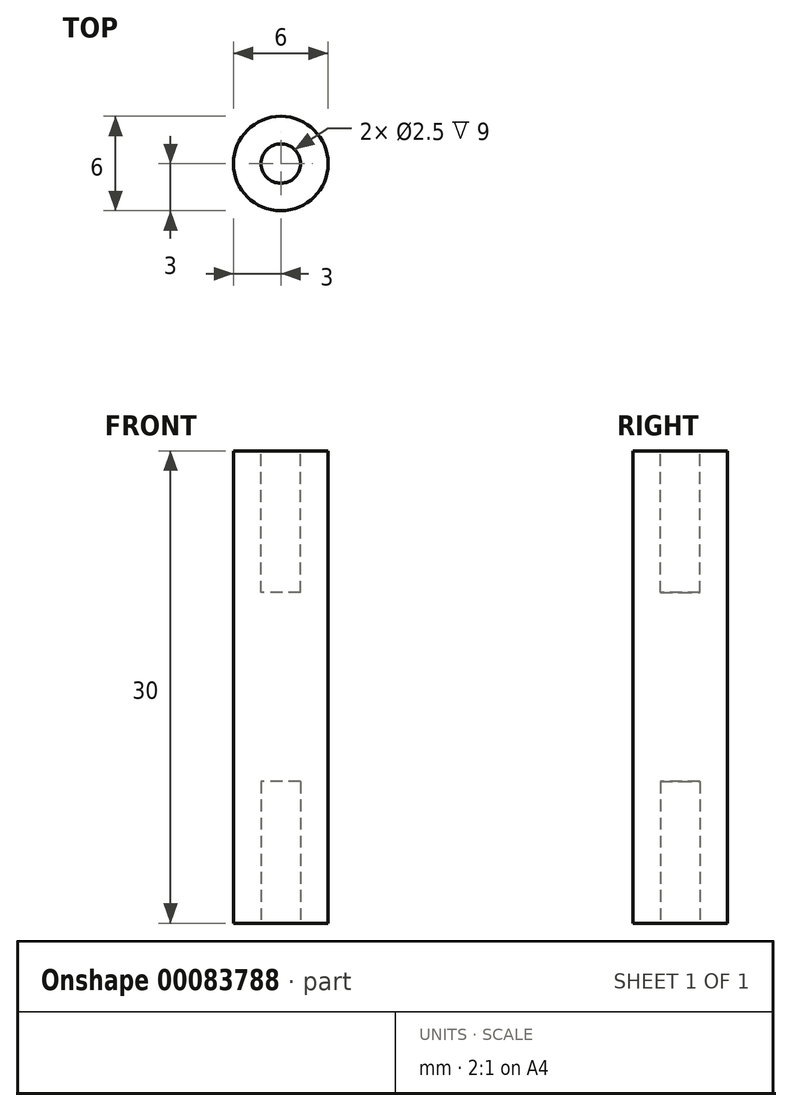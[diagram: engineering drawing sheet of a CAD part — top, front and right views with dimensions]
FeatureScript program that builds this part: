
annotation { "Feature Type Name" : "Feature", "Feature Type Description" : "" }
export const myFeature = defineFeature(function(context is Context, id is Id, definition is map)
    precondition{}
    {
        {
            var Q0;
            Q0=qCreatedBy(makeId("Top.planeOp"),FACE);
            var sketch = newSketch(context, id + "F0", { "sketchPlane" : qUnion([Q0])});
            skCircle(sketch, "E0", {"center": v(0, 0) * mm, "radius": 3 * mm});
            skCircle(sketch, "E1", {"center": v(0, 0) * mm, "radius": 1.25 * mm});
            skSolve(sketch);
        }
        {
            var Q0;
            Q0=makeQuery(id+"F0.imprint","IMPRINT",FACE,{"disambiguationData":[TD([[makeQuery(id+"F0.imprint","IMPRINT",EDGE,{"derivedFrom":sQuery(id+"F0.wireOp",EDGE,"E0")}),1.0]])]});
            var Q1;
            Q1=makeQuery(id+"F0.imprint","IMPRINT",FACE,{"disambiguationData":[TD([[makeQuery(id+"F0.imprint","IMPRINT",EDGE,{"derivedFrom":sQuery(id+"F0.wireOp",EDGE,"E1")}),1.0]])]});
            extrude(context, id + "F1", {"entities" : qUnion([Q0, Q1]), "depth" : 30 * mm});
        }
        {
            var Q0;
            Q0=makeQuery(id+"F0.imprint","IMPRINT",FACE,{"disambiguationData":[TD([[makeQuery(id+"F0.imprint","IMPRINT",EDGE,{"derivedFrom":sQuery(id+"F0.wireOp",EDGE,"E1")}),1.0]])]});
            extrude(context, id + "F2", {"entities" : qUnion([Q0]), "operationType" : NewBodyOperationType.REMOVE, "depth" : 9 * mm});
        }
        {
            var Q0;
            Q0=makeQuery(id+"F1.opExtrude","CAP_FACE",FACE,{"disambiguationData":[OSD([sQuery(id+"F0.wireOp",EDGE,"E0")])],"isStart":false});
            var sketch = newSketch(context, id + "F3", { "sketchPlane" : qUnion([Q0])});
            skCircle(sketch, "E2", {"center": v(0, 0) * mm, "radius": 1.25 * mm});
            skSolve(sketch);
        }
        {
            var Q0;
            Q0=makeQuery(id+"F3.imprint","IMPRINT",FACE,{"disambiguationData":[TD([[makeQuery(id+"F3.imprint","IMPRINT",EDGE,{"derivedFrom":sQuery(id+"F3.wireOp",EDGE,"E2")}),1.0]])]});
            extrude(context, id + "F4", {"entities" : qUnion([Q0]), "operationType" : NewBodyOperationType.REMOVE, "oppositeDirection" : true, "depth" : 9 * mm});
        }
    });
